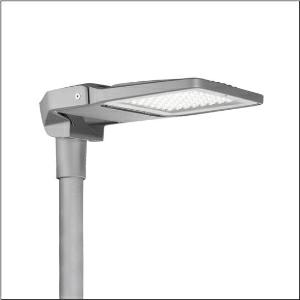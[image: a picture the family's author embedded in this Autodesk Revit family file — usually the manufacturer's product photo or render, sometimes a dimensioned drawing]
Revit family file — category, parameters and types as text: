
# Revit family: floodlight_fl_20_mini___pl43_5xa7672b2a4ac_47ff
name_source: partatom
category: Lighting Fixtures
units: mm (PartAtom-declared; Revit-internal decimal feet)

## family parameters
Cut with Voids When Loaded = No
Host = Face
Light Source = No
Part Type = Normal
Room Calculation Point = No
Round Connector Dimension = Use Diameter
Shared = No

## types (1)
- --- (1 x LED 4000K / CRI = 70 (unbekannt), 6650 lm, 4000K)
    Apparent Load = 51 VA
    CIE Flux Codes = 32 74 99 100 100
    Color Rendering = 70
    Color Temperature = 4000K
    Default Elevation = 1800 mm
    Description = Floodlight FL 20 mini, floodlight, primary light control with lens, of plastic, primary optical cover: protective disc, of toughened safety glass, transparent, light distribution: PL43, light emission: direct distribution, primary light characteristic: asymmetric, installation type: side-entry, post-top, LED, High Power LED, rated luminous flux: 6.650lm, luminous efficacy: 130lm/W, light colour: 740, colour temperature: 4000K, control gear: ECG Plus, control: flexible luminous flux parameterisation, time-dependent luminous flux control, digital communication interface, overheat protection, power reduction, electronic power reduction, with terminal, 5-pole, max. 2.5mm², mains connection: 220..240V, AC, 50/60Hz, rated input power: 51W, LED unit, of diecast aluminium, powder-coated, Siteco® metallic grey (DB 702S), corrosivity category C5 mid according to DIN EN ISO 12944, incl. 1x M20 cable gland for cable Ø 6.5..12mm, inclination adjustable: 0°, 5°, 10°, 15°, please order mast flange separately, length: 565mm, width: 335mm, height: 119mm, housing frame, of diecast aluminium, powder-coated, Siteco® metallic grey (DB 702S), mast flange adapter, of diecast aluminium, powder-coated, Siteco® metallic grey (DB 702S), DALI, protection rating (complete): IP66, insulation class (complete): insulation class II (safety insulation), certification: CE, ENEC, VDE, protection symbol: D, permissible operating ambient temperature: -40..+40°C, permissible operating ambient temperature for outdoor applications: -40..+50°C, standard: DIN EN 12944, packaging unit: 1 piece

Light Distribution: PL43
    Height = 62 mm  [stored 0.203412 ft]
    Lamp = 1 x LED 4000K / CRI >= 70 (unbekannt)
    Lamp Light Flux = 6650 lm
    Lamp count = 1
    Length = 565 mm
    Luminous efficacy = 130 lm/W
    Manufacturer = Siteco
    ModVariant = No
    Model = 5XA7672B2A4AC
    Number of Poles = 1
    OnlyDefault = Yes
    Power Factor = 1
    Product Name = Floodlight FL 20 mini | PL43
    Product group = floodlight | pylon top
    ProductGroupID = 6101
    Protection Class = Protection class II
    Protection Degree = IP 66
    RLX_Detail_Level = 1
    RLX_Emergency_Light_Flux = 0 lm
    RLX_Emergency_Type = 0
    RLX_Emergency_Type_DB = No
    RlxData = <blob elided: 101733 chars, md5=9b26e5fa>
    Socket = socket
    Standby Power = 0 W
    System Light Flux = 6650 lm
    System Power = 51 W
    Type Comments = factory setting: luminous flux: 100 % | dim-lin: 254 | 520 mA
    Type Image = l_1005946.jpg
    URL = http://relux.com
    VarID = @adj_164105
    Voltage = 0 V
    Weight = 0.00 kg
    Width = 335 mm

note: [stored X ft] marks values corroborated as IEEE doubles in the binary element streams (Revit-internal decimal feet)

## geometry (parser evidence)
native form markers: Blend x4, Sweep x12
no freeform markers — native parametric forms only
